# Revit family: P1036_3_Hole_Flat_Plate_Fitting
name_source: partatom
category: Generic Models
units: mm (PartAtom-declared; Revit-internal decimal feet)

## family parameters
Always vertical = No
Can host rebar = No
Cut with Voids When Loaded = No
OmniClass Number = 23.80.30.17.17
OmniClass Title = Cable Trays and Horizontal Racks
Part Type = Normal
Room Calculation Point = No
Round Connector Dimension = Use Diameter
Shared = No
Work Plane-Based = Yes

## types (9) — shared parameters
Center Distance = 0.813 "
Default Elevation = 48 "
Description = P1036 - 3 Hole Flat Plate Fitting
Disclaimer = http://www.unistrut.us
Hole Diameter = 0.563 "
LL = 1.875 "
Length = 3.5 "
Manufacturer = Atkore Unistrut
Model = P1036
Salsify ID1 = US-P1036
Thickness = 0.25 "
Type Comments = 80_77_27_15
URL = https://www.atkore.com

## per-type parameters (varying)
| type | Material | Power-Strut Part Number | UPC | Weight |
| P1036 EG | Electro Galvanized | PS 718 EG | "0786364103617" | 0.58 lbm |
| P1036 DF | Defender |  | "786364050867" | 0.61 lbm |
| P1036 HG | Hot Dip Galvanized | PS 718 HDG | "78636401605" | 0.61 lbm |
| P1036 GR | Green | PS 718 GRN | "78636410360" | 0.58 lbm |
| P1036 PL | Plain |  | "786364016061" | 0.58 lbm |
| P1036 AL | Aluminum |  | "786364016023" | 0.27 lbm |
| P1036 SS | Stainless Steel | PS 718 SS | "78636489058" | 0.58 lbm |
| P1036 ST | Stainless Steel |  | "786364051970" | 0.58 lbm |
| P1036 ZD | Zinc Dichromate | PS 718 ZD | "78636400720" | 0.58 lbm |

note: column(s) folded — value = type name in every type: Part Number

## geometry (parser evidence)
native form markers: Sweep x1
no freeform markers — native parametric forms only
